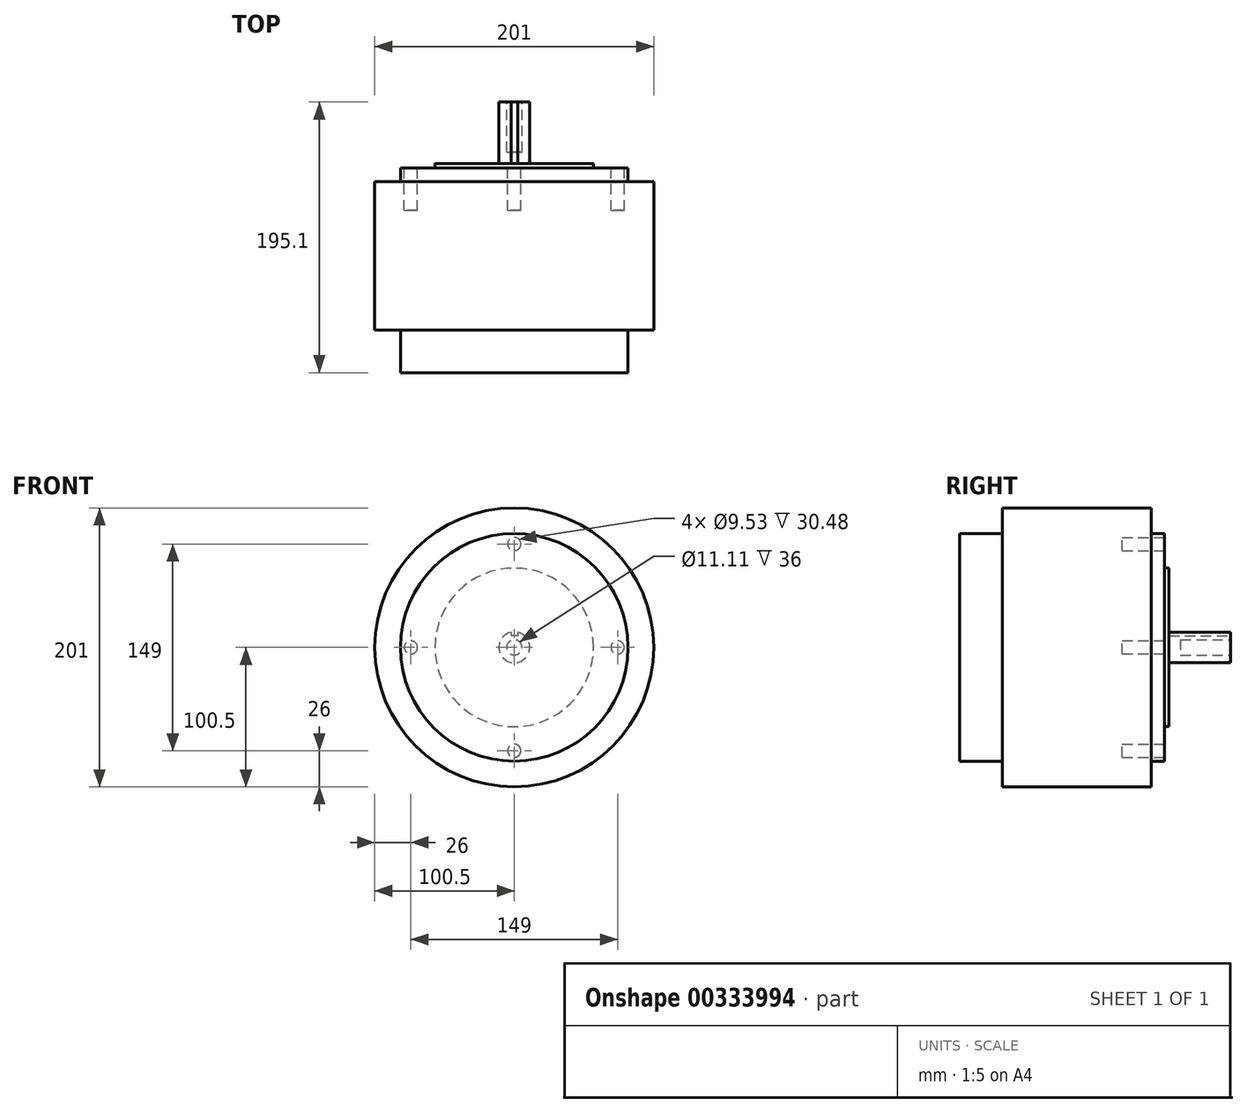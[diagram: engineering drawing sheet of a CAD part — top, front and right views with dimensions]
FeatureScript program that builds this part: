
annotation { "Feature Type Name" : "Feature", "Feature Type Description" : "" }
export const myFeature = defineFeature(function(context is Context, id is Id, definition is map)
    precondition{}
    {
        {
            var Q0;
            Q0=qCreatedBy(makeId("Front.planeOp"),FACE);
            var sketch = newSketch(context, id + "F0", { "sketchPlane" : qUnion([Q0])});
            skCircle(sketch, "E0", {"center": v(0, 0) * mm, "radius": 82 * mm});
            skSolve(sketch);
        }
        {
            var Q0;
            Q0 = qSketchRegion(id + "F0", true);
            extrude(context, id + "F1", {"entities" : qUnion([Q0]), "depth" : 147.5 * mm});
        }
        {
            var Q0;
            Q0=qCreatedBy(makeId("Front.planeOp"),FACE);
            cPlane(context, id + "F2", {"entities" : qUnion([Q0]), "cplaneType" : CPlaneType.OFFSET, "offset" : 9.65 * mm, "width" : 152.4 * mm, "height" : 152.4 * mm});
        }
        {
            var Q0;
            Q0=qCreatedBy(id+"F2.planeOp",FACE);
            var sketch = newSketch(context, id + "F3", { "sketchPlane" : qUnion([Q0])});
            skCircle(sketch, "E1", {"center": v(0, 0) * mm, "radius": 100.5 * mm});
            skSolve(sketch);
        }
        {
            var Q0;
            Q0 = qSketchRegion(id + "F3", true);
            extrude(context, id + "F4", {"entities" : qUnion([Q0]), "operationType" : NewBodyOperationType.ADD, "depth" : (107.5 - .38) * mm});
        }
        {
            var Q0;
            Q0=qCreatedBy(makeId("Front.planeOp"),FACE);
            var sketch = newSketch(context, id + "F5", { "sketchPlane" : qUnion([Q0])});
            skCircle(sketch, "E2", {"center": v(0, 0) * mm, "radius": 57.15 * mm});
            skSolve(sketch);
        }
        {
            var Q0;
            Q0 = qSketchRegion(id + "F5", true);
            extrude(context, id + "F6", {"entities" : qUnion([Q0]), "operationType" : NewBodyOperationType.ADD, "oppositeDirection" : true, "depth" : 3.2 * mm});
        }
        {
            var Q0;
            Q0=qCreatedBy(makeId("Front.planeOp"),FACE);
            var sketch = newSketch(context, id + "F7", { "sketchPlane" : qUnion([Q0])});
            skCircle(sketch, "E3", {"center": v(0, 0) * mm, "radius": 11.12 * mm});
            skSolve(sketch);
        }
        {
            var Q0;
            Q0 = qSketchRegion(id + "F7", true);
            extrude(context, id + "F8", {"entities" : qUnion([Q0]), "operationType" : NewBodyOperationType.ADD, "oppositeDirection" : true, "depth" : 47.6 * mm});
        }
        {
            var Q0;
            Q0=makeQuery(id+"F8.opExtrude","CAP_FACE",FACE,{"disambiguationData":[OSD([sQuery(id+"F7.wireOp",EDGE,"E3")])],"isStart":false});
            cPlane(context, id + "F9", {"entities" : qUnion([Q0]), "cplaneType" : CPlaneType.OFFSET, "offset" : 0 * mm, "width" : 152.4 * mm, "height" : 152.4 * mm});
        }
        {
            var Q0;
            Q0=qCreatedBy(id+"F9.planeOp",FACE);
            var sketch = newSketch(context, id + "F10", { "sketchPlane" : qUnion([Q0])});
            skLineSegment(sketch, "E4.bottom", {"start": v(-2.39, 11.85) * mm, "end": v(2.39, 11.85) * mm});
            skLineSegment(sketch, "E4.top", {"start": v(-2.4, 8.46) * mm, "end": v(2.4, 8.46) * mm});
            skLineSegment(sketch, "E4.left", {"start": v(-2.4, 11.85) * mm, "end": v(-2.4, 8.46) * mm});
            skLineSegment(sketch, "E4.right", {"start": v(2.39, 11.85) * mm, "end": v(2.39, 8.46) * mm});
            skPoint(sketch, "E5", {"position": v(0, 11.85) * mm});
            skPoint(sketch, "E6", {"position": v(0, 8.46) * mm});
            skPoint(sketch, "E7", {"position": v(0, -11.12) * mm});
            skSolve(sketch);
        }
        {
            var Q0;
            Q0 = qSketchRegion(id + "F10", true);
            var Q1;
            Q1=makeQuery(id+"F6.opExtrude","CAP_FACE",FACE,{"disambiguationData":[OSD([sQuery(id+"F5.wireOp",EDGE,"E2")])],"isStart":false});
            extrude(context, id + "F11", {"entities" : qUnion([Q0]), "operationType" : NewBodyOperationType.REMOVE, "endBound" : BoundingType.UP_TO_SURFACE, "oppositeDirection" : true, "endBoundEntityFace" : qUnion([Q1]), "depth" : 25.4 * mm});
        }
        {
            var Q0;
            Q0=qCreatedBy(id+"F9.planeOp",FACE);
            var sketch = newSketch(context, id + "F12", { "sketchPlane" : qUnion([Q0])});
            skCircle(sketch, "E8", {"center": v(0, 0) * mm, "radius": 5.56 * mm});
            skSolve(sketch);
        }
        {
            var Q0;
            Q0 = qSketchRegion(id + "F12", true);
            extrude(context, id + "F13", {"entities" : qUnion([Q0]), "operationType" : NewBodyOperationType.REMOVE, "oppositeDirection" : true, "depth" : 36 * mm});
        }
        {
            var Q0;
            Q0=qCreatedBy(makeId("Front.planeOp"),FACE);
            var sketch = newSketch(context, id + "F14", { "sketchPlane" : qUnion([Q0])});
            skCircle(sketch, "E9", {"center": v(0, 74.5) * mm, "radius": 4.76 * mm});
            skCircle(sketch, "E10.1.0", {"center": v(-74.5, 0) * mm, "radius": 4.76 * mm});
            skCircle(sketch, "E10.2.0", {"center": v(0, -74.5) * mm, "radius": 4.76 * mm});
            skCircle(sketch, "E10.3.0", {"center": v(74.5, 0) * mm, "radius": 4.76 * mm});
            skPoint(sketch, "E10.center", {"position": v(0, 0) * mm});
            skSolve(sketch);
        }
        {
            var Q0;
            Q0 = qSketchRegion(id + "F14", true);
            extrude(context, id + "F15", {"entities" : qUnion([Q0]), "operationType" : NewBodyOperationType.REMOVE, "depth" : 30.48 * mm});
        }
    });
